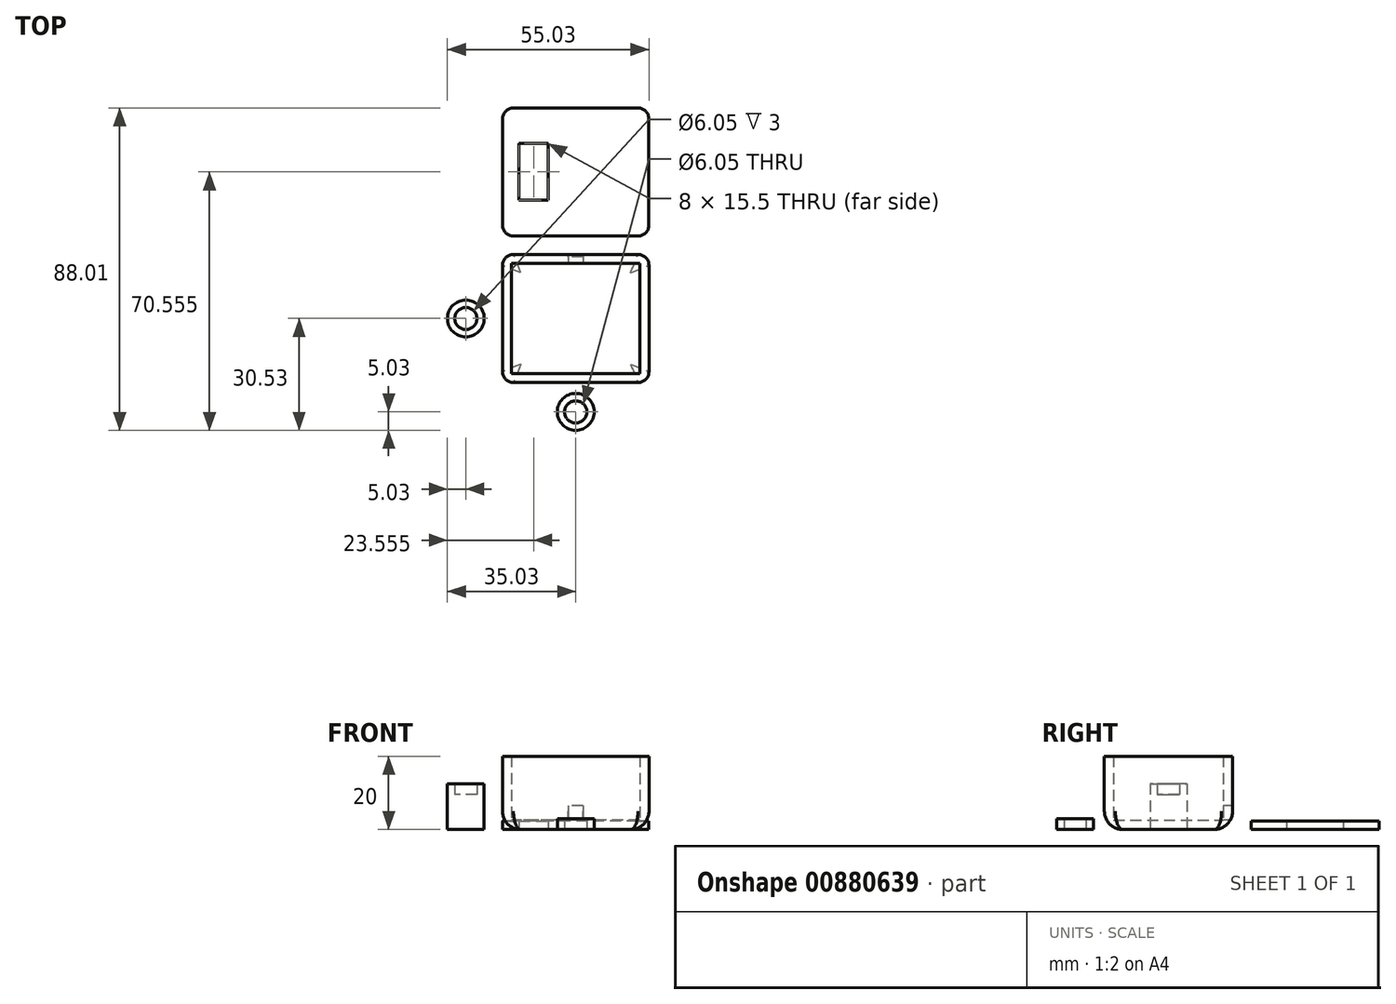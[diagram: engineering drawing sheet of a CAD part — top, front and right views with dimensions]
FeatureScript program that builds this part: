
annotation { "Feature Type Name" : "Feature", "Feature Type Description" : "" }
export const myFeature = defineFeature(function(context is Context, id is Id, definition is map)
    precondition{}
    {
        {
            var Q0;
            Q0=qCreatedBy(makeId("Top.planeOp"),FACE);
            var sketch = newSketch(context, id + "F0", { "sketchPlane" : qUnion([Q0])});
            skLineSegment(sketch, "E0.bottom", {"start": v(17.5, -15) * mm, "end": v(-17.5, -15) * mm});
            skLineSegment(sketch, "E0.top", {"start": v(17.5, 15) * mm, "end": v(-17.5, 15) * mm});
            skLineSegment(sketch, "E0.left", {"start": v(17.5, -15) * mm, "end": v(17.5, 15) * mm});
            skLineSegment(sketch, "E0.right", {"start": v(-17.5, -15) * mm, "end": v(-17.5, 15) * mm});
            skPoint(sketch, "E0.middle", {"position": v(0, 0) * mm});
            skLineSegment(sketch, "E1.bottom", {"start": v(-15.5, 7.75) * mm, "end": v(-7.5, 7.75) * mm});
            skLineSegment(sketch, "E1.top", {"start": v(-15.5, -7.75) * mm, "end": v(-7.5, -7.75) * mm});
            skLineSegment(sketch, "E1.left", {"start": v(-15.5, 7.75) * mm, "end": v(-15.5, -7.75) * mm});
            skLineSegment(sketch, "E1.right", {"start": v(-7.5, 7.75) * mm, "end": v(-7.5, -7.75) * mm});
            skLineSegment(sketch, "E2.0", {"start": v(17, 17.5) * mm, "end": v(-17, 17.5) * mm});
            skLineSegment(sketch, "E2.1", {"start": v(20, -14.5) * mm, "end": v(20, 14.5) * mm});
            skLineSegment(sketch, "E2.2", {"start": v(17, -17.5) * mm, "end": v(-17, -17.5) * mm});
            skLineSegment(sketch, "E2.3", {"start": v(-20, -14.5) * mm, "end": v(-20, 14.5) * mm});
            skPoint(sketch, "E3.visualSharp", {"position": v(20, 17.5) * mm});
            skArc(sketch, "E3.filletArc", {"start": v(20, 14.5) * mm, "mid": v(19.12, 16.62) * mm, "end": v(17, 17.5) * mm});
            skPoint(sketch, "E4.visualSharp", {"position": v(20, -17.5) * mm});
            skArc(sketch, "E4.filletArc", {"start": v(17, -17.5) * mm, "mid": v(19.12, -16.62) * mm, "end": v(20, -14.5) * mm});
            skPoint(sketch, "E5.visualSharp", {"position": v(-20, -17.5) * mm});
            skArc(sketch, "E5.filletArc", {"start": v(-20, -14.5) * mm, "mid": v(-19.12, -16.62) * mm, "end": v(-17, -17.5) * mm});
            skPoint(sketch, "E6.visualSharp", {"position": v(-20, 17.5) * mm});
            skArc(sketch, "E6.filletArc", {"start": v(-17, 17.5) * mm, "mid": v(-19.12, 16.62) * mm, "end": v(-20, 14.5) * mm});
            skLineSegment(sketch, "E7.bottom", {"start": v(-2, 17.5) * mm, "end": v(2, 17.5) * mm});
            skLineSegment(sketch, "E7.top", {"start": v(-2, 15) * mm, "end": v(2, 15) * mm});
            skLineSegment(sketch, "E7.left", {"start": v(-2, 17.5) * mm, "end": v(-2, 15) * mm});
            skLineSegment(sketch, "E7.right", {"start": v(2, 17.5) * mm, "end": v(2, 15) * mm});
            skSolve(sketch);
        }
        {
            var Q0;
            Q0=makeQuery(id+"F0.imprint","IMPRINT",FACE,{"disambiguationData":[TD([[makeQuery(id+"F0.imprint","IMPRINT",EDGE,{"derivedFrom":sQuery(id+"F0.wireOp",EDGE,"E0.bottom")}),1.0]])]});
            extrude(context, id + "F1", {"entities" : qUnion([Q0]), "depth" : 20 * mm, "offsetDistance" : 25 * mm});
        }
        {
            var Q0;
            Q0=qCreatedBy(makeId("Top.planeOp"),FACE);
            var sketch = newSketch(context, id + "F2", { "sketchPlane" : qUnion([Q0])});
            skLineSegment(sketch, "E8.bottom", {"start": v(17.5, -15) * mm, "end": v(-17.5, -15) * mm});
            skLineSegment(sketch, "E8.top", {"start": v(17.5, 15) * mm, "end": v(-17.5, 15) * mm});
            skLineSegment(sketch, "E8.left", {"start": v(17.5, -15) * mm, "end": v(17.5, 15) * mm});
            skLineSegment(sketch, "E8.right", {"start": v(-17.5, -15) * mm, "end": v(-17.5, 15) * mm});
            skPoint(sketch, "E8.middle", {"position": v(0, 0) * mm});
            skLineSegment(sketch, "E9.bottom", {"start": v(-15.5, 7.75) * mm, "end": v(-7.5, 7.75) * mm});
            skLineSegment(sketch, "E9.top", {"start": v(-15.5, -7.75) * mm, "end": v(-7.5, -7.75) * mm});
            skLineSegment(sketch, "E9.left", {"start": v(-15.5, 7.75) * mm, "end": v(-15.5, -7.75) * mm});
            skLineSegment(sketch, "E9.right", {"start": v(-7.5, 7.75) * mm, "end": v(-7.5, -7.75) * mm});
            skLineSegment(sketch, "E10.0", {"start": v(17, 17.5) * mm, "end": v(-17, 17.5) * mm});
            skLineSegment(sketch, "E10.1", {"start": v(20, -14.5) * mm, "end": v(20, 14.5) * mm});
            skLineSegment(sketch, "E10.2", {"start": v(17, -17.5) * mm, "end": v(-17, -17.5) * mm});
            skLineSegment(sketch, "E10.3", {"start": v(-20, -14.5) * mm, "end": v(-20, 14.5) * mm});
            skPoint(sketch, "E11.visualSharp", {"position": v(20, 17.5) * mm});
            skArc(sketch, "E11.filletArc", {"start": v(20, 14.5) * mm, "mid": v(19.12, 16.62) * mm, "end": v(17, 17.5) * mm});
            skPoint(sketch, "E12.visualSharp", {"position": v(20, -17.5) * mm});
            skArc(sketch, "E12.filletArc", {"start": v(17, -17.5) * mm, "mid": v(19.12, -16.62) * mm, "end": v(20, -14.5) * mm});
            skPoint(sketch, "E13.visualSharp", {"position": v(-20, -17.5) * mm});
            skArc(sketch, "E13.filletArc", {"start": v(-20, -14.5) * mm, "mid": v(-19.12, -16.62) * mm, "end": v(-17, -17.5) * mm});
            skPoint(sketch, "E14.visualSharp", {"position": v(-20, 17.5) * mm});
            skArc(sketch, "E14.filletArc", {"start": v(-17, 17.5) * mm, "mid": v(-19.12, 16.62) * mm, "end": v(-20, 14.5) * mm});
            skLineSegment(sketch, "E15.bottom", {"start": v(-2, 17.5) * mm, "end": v(2, 17.5) * mm});
            skLineSegment(sketch, "E15.top", {"start": v(-2, 15) * mm, "end": v(2, 15) * mm});
            skLineSegment(sketch, "E15.left", {"start": v(-2, 17.5) * mm, "end": v(-2, 15) * mm});
            skLineSegment(sketch, "E15.right", {"start": v(2, 17.5) * mm, "end": v(2, 15) * mm});
            skSolve(sketch);
        }
        {
            var Q0;
            Q0=makeQuery(id+"F2.imprint","IMPRINT",FACE,{"disambiguationData":[TD([[makeQuery(id+"F2.imprint","IMPRINT",EDGE,{"derivedFrom":sQuery(id+"F2.wireOp",EDGE,"E8.bottom")}),-1.0]])]});
            var Q1;
            {var subQ0=sQuery(id+"F2.wireOp",EDGE,"E15.left");Q1=makeQuery(id+"F2.imprint","IMPRINT",FACE,{"disambiguationData":[TD([[makeQuery(id+"F2.imprint","IMPRINT",EDGE,{"derivedFrom":subQ0}),1.0]])]});}
            var Q2;
            Q2=makeQuery(id+"F2.imprint","IMPRINT",FACE,{"disambiguationData":[TD([[makeQuery(id+"F2.imprint","IMPRINT",EDGE,{"derivedFrom":sQuery(id+"F2.wireOp",EDGE,"E9.bottom")}),-1.0]])]});
            extrude(context, id + "F3", {"entities" : qUnion([Q0, Q1, Q2]), "operationType" : NewBodyOperationType.ADD, "depth" : 2.5 * mm, "offsetDistance" : 25 * mm});
        }
        {
            var Q0;
            Q0=qCreatedBy(makeId("Top.planeOp"),FACE);
            var sketch = newSketch(context, id + "F4", { "sketchPlane" : qUnion([Q0])});
            skLineSegment(sketch, "E16.bottom", {"start": v(17.5, -15) * mm, "end": v(-17.5, -15) * mm});
            skLineSegment(sketch, "E16.top", {"start": v(17.5, 15) * mm, "end": v(-17.5, 15) * mm});
            skLineSegment(sketch, "E16.left", {"start": v(17.5, -15) * mm, "end": v(17.5, 15) * mm});
            skLineSegment(sketch, "E16.right", {"start": v(-17.5, -15) * mm, "end": v(-17.5, 15) * mm});
            skPoint(sketch, "E16.middle", {"position": v(0, 0) * mm});
            skLineSegment(sketch, "E17.bottom", {"start": v(-15.5, 7.75) * mm, "end": v(-7.5, 7.75) * mm});
            skLineSegment(sketch, "E17.top", {"start": v(-15.5, -7.75) * mm, "end": v(-7.5, -7.75) * mm});
            skLineSegment(sketch, "E17.left", {"start": v(-15.5, 7.75) * mm, "end": v(-15.5, -7.75) * mm});
            skLineSegment(sketch, "E17.right", {"start": v(-7.5, 7.75) * mm, "end": v(-7.5, -7.75) * mm});
            skLineSegment(sketch, "E18.0", {"start": v(17, 17.5) * mm, "end": v(-17, 17.5) * mm});
            skLineSegment(sketch, "E18.1", {"start": v(20, -14.5) * mm, "end": v(20, 14.5) * mm});
            skLineSegment(sketch, "E18.2", {"start": v(17, -17.5) * mm, "end": v(-17, -17.5) * mm});
            skLineSegment(sketch, "E18.3", {"start": v(-20, -14.5) * mm, "end": v(-20, 14.5) * mm});
            skPoint(sketch, "E19.visualSharp", {"position": v(20, 17.5) * mm});
            skArc(sketch, "E19.filletArc", {"start": v(20, 14.5) * mm, "mid": v(19.12, 16.62) * mm, "end": v(17, 17.5) * mm});
            skPoint(sketch, "E20.visualSharp", {"position": v(20, -17.5) * mm});
            skArc(sketch, "E20.filletArc", {"start": v(17, -17.5) * mm, "mid": v(19.12, -16.62) * mm, "end": v(20, -14.5) * mm});
            skPoint(sketch, "E21.visualSharp", {"position": v(-20, -17.5) * mm});
            skArc(sketch, "E21.filletArc", {"start": v(-20, -14.5) * mm, "mid": v(-19.12, -16.62) * mm, "end": v(-17, -17.5) * mm});
            skPoint(sketch, "E22.visualSharp", {"position": v(-20, 17.5) * mm});
            skArc(sketch, "E22.filletArc", {"start": v(-17, 17.5) * mm, "mid": v(-19.12, 16.62) * mm, "end": v(-20, 14.5) * mm});
            skLineSegment(sketch, "E23.bottom", {"start": v(-2, 17.5) * mm, "end": v(2, 17.5) * mm});
            skLineSegment(sketch, "E23.top", {"start": v(-2, 15) * mm, "end": v(2, 15) * mm});
            skLineSegment(sketch, "E23.left", {"start": v(-2, 17.5) * mm, "end": v(-2, 15) * mm});
            skLineSegment(sketch, "E23.right", {"start": v(2, 17.5) * mm, "end": v(2, 15) * mm});
            skSolve(sketch);
        }
        {
            var Q0;
            {var subQ0=sQuery(id+"F4.wireOp",EDGE,"E23.left");Q0=makeQuery(id+"F4.imprint","IMPRINT",FACE,{"disambiguationData":[TD([[makeQuery(id+"F4.imprint","IMPRINT",EDGE,{"derivedFrom":subQ0}),1.0]])]});}
            extrude(context, id + "F5", {"entities" : qUnion([Q0]), "operationType" : NewBodyOperationType.ADD, "depth" : 20 * mm, "offsetDistance" : 25 * mm, "hasSecondDirection" : true, "secondDirectionOppositeDirection" : false, "secondDirectionDepth" : 6.5 * mm});
        }
        {
            var Q0;
            Q0=qCreatedBy(makeId("Top.planeOp"),FACE);
            var sketch = newSketch(context, id + "F6", { "sketchPlane" : qUnion([Q0])});
            skLineSegment(sketch, "E24.bottom", {"start": v(17.47, 25.03) * mm, "end": v(-17.48, 25.02) * mm});
            skLineSegment(sketch, "E24.top", {"start": v(17.47, 54.98) * mm, "end": v(-17.48, 54.97) * mm});
            skLineSegment(sketch, "E24.left", {"start": v(17.47, 25.03) * mm, "end": v(17.47, 54.98) * mm});
            skLineSegment(sketch, "E24.right", {"start": v(-17.48, 25.02) * mm, "end": v(-17.48, 54.97) * mm});
            skPoint(sketch, "E24.middle", {"position": v(0, 40) * mm});
            skLineSegment(sketch, "E25.bottom", {"start": v(-15.48, 47.77) * mm, "end": v(-7.48, 47.77) * mm});
            skLineSegment(sketch, "E25.top", {"start": v(-15.48, 32.27) * mm, "end": v(-7.48, 32.27) * mm});
            skLineSegment(sketch, "E25.left", {"start": v(-15.48, 47.77) * mm, "end": v(-15.48, 32.27) * mm});
            skLineSegment(sketch, "E25.right", {"start": v(-7.48, 47.77) * mm, "end": v(-7.48, 32.27) * mm});
            skLineSegment(sketch, "E26.0", {"start": v(16.97, 57.48) * mm, "end": v(-16.98, 57.48) * mm});
            skLineSegment(sketch, "E26.1", {"start": v(19.98, 25.53) * mm, "end": v(19.97, 54.48) * mm});
            skLineSegment(sketch, "E26.2", {"start": v(16.98, 22.53) * mm, "end": v(-16.98, 22.52) * mm});
            skLineSegment(sketch, "E26.3", {"start": v(-19.98, 25.52) * mm, "end": v(-19.98, 54.47) * mm});
            skPoint(sketch, "E27.visualSharp", {"position": v(19.97, 57.48) * mm});
            skArc(sketch, "E27.filletArc", {"start": v(19.97, 54.48) * mm, "mid": v(19.1, 56.6) * mm, "end": v(16.97, 57.48) * mm});
            skPoint(sketch, "E28.visualSharp", {"position": v(19.98, 22.53) * mm});
            skArc(sketch, "E28.filletArc", {"start": v(16.98, 22.53) * mm, "mid": v(19.1, 23.4) * mm, "end": v(19.98, 25.53) * mm});
            skPoint(sketch, "E29.visualSharp", {"position": v(-19.98, 22.52) * mm});
            skArc(sketch, "E29.filletArc", {"start": v(-19.98, 25.52) * mm, "mid": v(-19.1, 23.4) * mm, "end": v(-16.98, 22.52) * mm});
            skPoint(sketch, "E30.visualSharp", {"position": v(-19.98, 57.48) * mm});
            skArc(sketch, "E30.filletArc", {"start": v(-16.98, 57.48) * mm, "mid": v(-19.1, 56.6) * mm, "end": v(-19.98, 54.47) * mm});
            skLineSegment(sketch, "E31.bottom", {"start": v(-1.98, 57.48) * mm, "end": v(2.02, 57.48) * mm});
            skLineSegment(sketch, "E31.top", {"start": v(-1.98, 54.98) * mm, "end": v(2.02, 54.98) * mm});
            skLineSegment(sketch, "E31.left", {"start": v(-1.98, 57.48) * mm, "end": v(-1.98, 54.98) * mm});
            skLineSegment(sketch, "E31.right", {"start": v(2.02, 57.48) * mm, "end": v(2.02, 54.98) * mm});
            skSolve(sketch);
        }
        {
            var Q0;
            Q0=makeQuery(id+"F6.imprint","IMPRINT",FACE,{"disambiguationData":[TD([[makeQuery(id+"F6.imprint","IMPRINT",EDGE,{"derivedFrom":sQuery(id+"F6.wireOp",EDGE,"E24.bottom")}),-1.0]])]});
            var Q1;
            Q1=makeQuery(id+"F6.imprint","IMPRINT",FACE,{"disambiguationData":[TD([[makeQuery(id+"F6.imprint","IMPRINT",EDGE,{"derivedFrom":sQuery(id+"F6.wireOp",EDGE,"E24.bottom")}),1.0]])]});
            var Q2;
            {var subQ0=sQuery(id+"F6.wireOp",EDGE,"E31.left");Q2=makeQuery(id+"F6.imprint","IMPRINT",FACE,{"disambiguationData":[TD([[makeQuery(id+"F6.imprint","IMPRINT",EDGE,{"derivedFrom":subQ0}),1.0]])]});}
            extrude(context, id + "F7", {"entities" : qUnion([Q0, Q1, Q2]), "depth" : 2.25 * mm, "offsetDistance" : 25 * mm});
        }
        {
            var Q0;
            Q0=qCreatedBy(makeId("Top.planeOp"),FACE);
            var sketch = newSketch(context, id + "F8", { "sketchPlane" : qUnion([Q0])});
            skCircle(sketch, "E32", {"center": v(-30, 0) * mm, "radius": 3.02 * mm});
            skCircle(sketch, "E33.0", {"center": v(-30, 0) * mm, "radius": 5.03 * mm});
            skSolve(sketch);
        }
        {
            var Q0;
            Q0=makeQuery(id+"F8.imprint","IMPRINT",FACE,{"disambiguationData":[TD([[makeQuery(id+"F8.imprint","IMPRINT",EDGE,{"derivedFrom":sQuery(id+"F8.wireOp",EDGE,"E32")}),-1.0]])]});
            extrude(context, id + "F9", {"entities" : qUnion([Q0]), "depth" : 12.5 * mm, "offsetDistance" : 25 * mm});
        }
        {
            var Q0;
            Q0=qCreatedBy(makeId("Top.planeOp"),FACE);
            var sketch = newSketch(context, id + "F10", { "sketchPlane" : qUnion([Q0])});
            skCircle(sketch, "E34", {"center": v(-30, 0) * mm, "radius": 3.02 * mm});
            skCircle(sketch, "E35.0", {"center": v(-30, 0) * mm, "radius": 5.03 * mm});
            skSolve(sketch);
        }
        {
            var Q0;
            Q0=makeQuery(id+"F10.imprint","IMPRINT",FACE,{"disambiguationData":[TD([[makeQuery(id+"F10.imprint","IMPRINT",EDGE,{"derivedFrom":sQuery(id+"F10.wireOp",EDGE,"E34")}),1.0]])]});
            extrude(context, id + "F11", {"entities" : qUnion([Q0]), "operationType" : NewBodyOperationType.ADD, "depth" : 9.5 * mm, "offsetDistance" : 25 * mm});
        }
        {
            var Q0;
            Q0=makeQuery(id+"F1.opExtrude","CAP_EDGE",EDGE,{"disambiguationData":[OSD([sQuery(id+"F0.wireOp",EDGE,"E2.2")])],"isStart":true});
            fillet(context, id + "F12", {"entities" : qUnion([Q0]), "radius" : 5 * mm, "tangentPropagation" : true, "allowEdgeOverflow" : false});
        }
        {
            var Q0;
            Q0=qCreatedBy(makeId("Top.planeOp"),FACE);
            var sketch = newSketch(context, id + "F13", { "sketchPlane" : qUnion([Q0])});
            skCircle(sketch, "E36", {"center": v(0, -25.5) * mm, "radius": 3.02 * mm});
            skCircle(sketch, "E37.0", {"center": v(0, -25.5) * mm, "radius": 5.03 * mm});
            skSolve(sketch);
        }
        {
            var Q0;
            Q0=makeQuery(id+"F13.imprint","IMPRINT",FACE,{"disambiguationData":[TD([[makeQuery(id+"F13.imprint","IMPRINT",EDGE,{"derivedFrom":sQuery(id+"F13.wireOp",EDGE,"E36")}),-1.0]])]});
            extrude(context, id + "F14", {"entities" : qUnion([Q0]), "depth" : 3 * mm, "offsetDistance" : 25 * mm});
        }
    });
